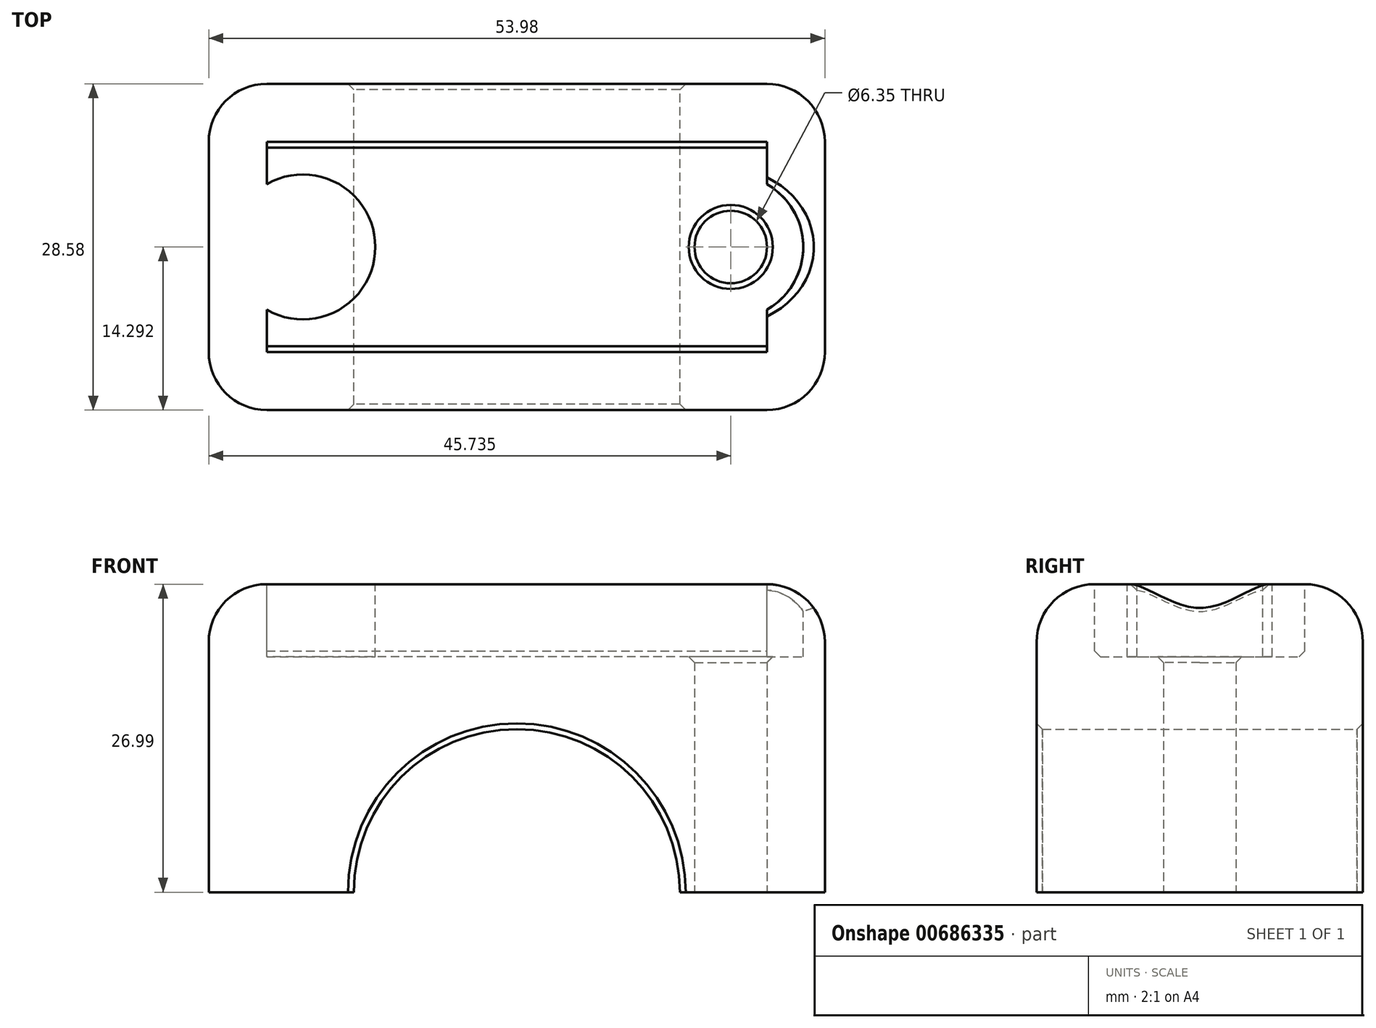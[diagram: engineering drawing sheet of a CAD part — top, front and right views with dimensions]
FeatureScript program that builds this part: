
annotation { "Feature Type Name" : "Feature", "Feature Type Description" : "" }
export const myFeature = defineFeature(function(context is Context, id is Id, definition is map)
    precondition{}
    {
        {
            var Q0;
            Q0=qCreatedBy(makeId("Front.planeOp"),FACE);
            var sketch = newSketch(context, id + "F0", { "sketchPlane" : qUnion([Q0])});
            skArc(sketch, "E0", {"start": v(14.29, 0) * mm, "mid": v(0, 14.29) * mm, "end": v(-14.29, 0) * mm});
            skLineSegment(sketch, "E1", {"start": v(-26.99, 0) * mm, "end": v(-26.99, 26.99) * mm});
            skLineSegment(sketch, "E2", {"start": v(-26.99, 26.99) * mm, "end": v(26.99, 26.99) * mm});
            skLineSegment(sketch, "E3", {"start": v(26.99, 26.99) * mm, "end": v(26.99, 0) * mm});
            skLineSegment(sketch, "E4.trimOffspring", {"start": v(-14.29, 0) * mm, "end": v(-26.99, 0) * mm});
            skLineSegment(sketch, "E5", {"start": v(14.29, 0) * mm, "end": v(26.99, 0) * mm});
            skSolve(sketch);
        }
        {
            var Q0;
            Q0 = qSketchRegion(id + "F0", true);
            extrude(context, id + "F1", {"entities" : qUnion([Q0]), "depth" : 28.57 * mm, "offsetDistance" : 25.4 * mm});
        }
        {
            var Q0;
            Q0=makeQuery(id+"F1.opExtrude","CAP_EDGE",EDGE,{"disambiguationData":[OSD([sQuery(id+"F0.wireOp",EDGE,"E1")])],"isStart":false});
            var Q1;
            Q1=makeQuery(id+"F1.opExtrude","CAP_EDGE",EDGE,{"disambiguationData":[OSD([sQuery(id+"F0.wireOp",EDGE,"E1")])],"isStart":true});
            var Q2;
            Q2=makeQuery(id+"F1.opExtrude","SWEPT_EDGE",EDGE,{"disambiguationData":[OSD([sQuery(id+"F0.wireOp",EDGE,"E1"),sQuery(id+"F0.wireOp",EDGE,"E2")])]});
            var Q3;
            Q3=makeQuery(id+"F1.opExtrude","CAP_EDGE",EDGE,{"disambiguationData":[OSD([sQuery(id+"F0.wireOp",EDGE,"E2")])],"isStart":true});
            var Q4;
            Q4=makeQuery(id+"F1.opExtrude","CAP_EDGE",EDGE,{"disambiguationData":[OSD([sQuery(id+"F0.wireOp",EDGE,"E3")])],"isStart":true});
            var Q5;
            Q5=makeQuery(id+"F1.opExtrude","SWEPT_EDGE",EDGE,{"disambiguationData":[OSD([sQuery(id+"F0.wireOp",EDGE,"E2"),sQuery(id+"F0.wireOp",EDGE,"E3")])]});
            var Q6;
            Q6=makeQuery(id+"F1.opExtrude","CAP_EDGE",EDGE,{"disambiguationData":[OSD([sQuery(id+"F0.wireOp",EDGE,"E3")])],"isStart":false});
            var Q7;
            Q7=makeQuery(id+"F1.opExtrude","CAP_EDGE",EDGE,{"disambiguationData":[OSD([sQuery(id+"F0.wireOp",EDGE,"E2")])],"isStart":false});
            fillet(context, id + "F2", {"entities" : qUnion([Q0, Q1, Q2, Q3, Q4, Q5, Q6, Q7]), "radius" : 5.08 * mm, "tangentPropagation" : true, "allowEdgeOverflow" : false});
        }
        {
            var Q0;
            Q0=makeQuery(id+"F1.opExtrude","CAP_EDGE",EDGE,{"disambiguationData":[OSD([sQuery(id+"F0.wireOp",EDGE,"E0")])],"isStart":false});
            var Q1;
            Q1=makeQuery(id+"F1.opExtrude","CAP_EDGE",EDGE,{"disambiguationData":[OSD([sQuery(id+"F0.wireOp",EDGE,"E0")])],"isStart":true});
            chamfer(context, id + "F3", {"entities" : qUnion([Q0, Q1]), "width" : 0.5 * mm, "tangentPropagation" : true});
        }
        {
            var Q0;
            Q0=makeQuery(id+"F1.opExtrude","SWEPT_FACE",FACE,{"disambiguationData":[OSD([sQuery(id+"F0.wireOp",EDGE,"E5")])]});
            var sketch = newSketch(context, id + "F4", { "sketchPlane" : qUnion([Q0])});
            skLineSegment(sketch, "E6", {"start": v(14.29, 14.29) * mm, "end": v(30.3, 14.29) * mm, "construction": true});
            skLineSegment(sketch, "E7", {"start": v(0, 0) * mm, "end": v(0, -7.99) * mm, "construction": true});
            skCircle(sketch, "E8", {"center": v(18.75, 14.29) * mm, "radius": 3.18 * mm});
            skCircle(sketch, "E9.MirrorC", {"center": v(-18.75, 14.29) * mm, "radius": 3.18 * mm});
            skSolve(sketch);
        }
        {
            var Q0;
            Q0=makeQuery(id+"F4.imprint","IMPRINT",FACE,{"disambiguationData":[TD([[makeQuery(id+"F4.imprint","IMPRINT",EDGE,{"derivedFrom":sQuery(id+"F4.wireOp",EDGE,"E8")}),1.0]])]});
            var Q1;
            Q1=makeQuery(id+"F4.imprint","IMPRINT",FACE,{"disambiguationData":[TD([[makeQuery(id+"F4.imprint","IMPRINT",EDGE,{"derivedFrom":sQuery(id+"F4.wireOp",EDGE,"E9.MirrorC")}),-1.0]])]});
            extrude(context, id + "F5", {"entities" : qUnion([Q0, Q1]), "operationType" : NewBodyOperationType.REMOVE, "oppositeDirection" : true, "depth" : 34.04 * mm, "offsetDistance" : 25.4 * mm});
        }
        {
            var Q0;
            Q0=makeQuery(id+"F1.opExtrude","SWEPT_FACE",FACE,{"disambiguationData":[OSD([sQuery(id+"F0.wireOp",EDGE,"E2")])]});
            var sketch = newSketch(context, id + "F6", { "sketchPlane" : qUnion([Q0])});
            skCircle(sketch, "E10", {"center": v(18.75, -14.29) * mm, "radius": 6.35 * mm});
            skLineSegment(sketch, "E11", {"start": v(0, -19.6) * mm, "end": v(0, 0) * mm, "construction": true});
            skCircle(sketch, "E12.MirrorC", {"center": v(-18.75, -14.29) * mm, "radius": 6.35 * mm});
            skSolve(sketch);
        }
        {
            var Q0;
            {var subQ0=sQuery(id+"F6.wireOp",EDGE,"E12.MirrorC");var subQ1=sQuery(id+"F0.wireOp",EDGE,"E2");var subQ2=makeQuery(id+"F2.opFillet","BLEND_EDGE",EDGE,{"blendedFrom":[makeQuery(id+"F1.opExtrude","SWEPT_EDGE",EDGE,{"disambiguationData":[OSD([sQuery(id+"F0.wireOp",EDGE,"E1"),subQ1])]}),makeQuery(id+"F1.opExtrude","SWEPT_FACE",FACE,{"disambiguationData":[OSD([subQ1])]})],"blendedInto":[makeQuery(id+"F1.opExtrude","SWEPT_FACE",FACE,{"disambiguationData":[OSD([subQ1])]})]});var subQ3=makeQuery(id+"F6.imprint","INTERSECT",VERTEX,{"disambiguationData":[OD(0.0)],"derivedFrom":[subQ2,subQ0]});Q0=makeQuery(id+"F6.imprint","IMPRINT",FACE,{"disambiguationData":[TD([[makeQuery(id+"F6.imprint","IMPRINT",EDGE,{"disambiguationData":[TD([[subQ3,1.0]])],"derivedFrom":subQ0}),-1.0]])]});}
            var Q1;
            {var subQ1=sQuery(id+"F0.wireOp",EDGE,"E2");var subQ2=makeQuery(id+"F1.opExtrude","SWEPT_FACE",FACE,{"disambiguationData":[OSD([subQ1])]});Q1=makeQuery(id+"F6.imprint","IMPRINT",FACE,{"disambiguationData":[TD([[makeQuery(id+"F6.imprint","IMPRINT",EDGE,{"derivedFrom":makeQuery(id+"F5.boolean.opBoolean","INTERSECT",EDGE,{"derivedFrom":[subQ2,makeQuery(id+"F5.opExtrude","SWEPT_FACE",FACE,{"disambiguationData":[OSD([sQuery(id+"F4.wireOp",EDGE,"E8")])]})]})}),-1.0]])]});}
            var Q2;
            {var subQ0=sQuery(id+"F6.wireOp",EDGE,"E10");var subQ1=sQuery(id+"F0.wireOp",EDGE,"E2");var subQ2=makeQuery(id+"F2.opFillet","BLEND_EDGE",EDGE,{"blendedFrom":[makeQuery(id+"F1.opExtrude","SWEPT_EDGE",EDGE,{"disambiguationData":[OSD([subQ1,sQuery(id+"F0.wireOp",EDGE,"E3")])]}),makeQuery(id+"F1.opExtrude","SWEPT_FACE",FACE,{"disambiguationData":[OSD([subQ1])]})],"blendedInto":[makeQuery(id+"F1.opExtrude","SWEPT_FACE",FACE,{"disambiguationData":[OSD([subQ1])]})]});var subQ3=makeQuery(id+"F6.imprint","INTERSECT",VERTEX,{"disambiguationData":[OD(0.0)],"derivedFrom":[subQ2,subQ0]});Q2=makeQuery(id+"F6.imprint","IMPRINT",FACE,{"disambiguationData":[TD([[makeQuery(id+"F6.imprint","IMPRINT",EDGE,{"disambiguationData":[TD([[subQ3,1.0]])],"derivedFrom":subQ0}),1.0]])]});}
            var Q3;
            {var subQ1=sQuery(id+"F0.wireOp",EDGE,"E2");var subQ2=makeQuery(id+"F1.opExtrude","SWEPT_FACE",FACE,{"disambiguationData":[OSD([subQ1])]});Q3=makeQuery(id+"F6.imprint","IMPRINT",FACE,{"disambiguationData":[TD([[makeQuery(id+"F6.imprint","IMPRINT",EDGE,{"derivedFrom":makeQuery(id+"F5.boolean.opBoolean","INTERSECT",EDGE,{"derivedFrom":[subQ2,makeQuery(id+"F5.opExtrude","SWEPT_FACE",FACE,{"disambiguationData":[OSD([sQuery(id+"F4.wireOp",EDGE,"E9.MirrorC")])]})]})}),1.0]])]});}
            extrude(context, id + "F7", {"entities" : qUnion([Q0, Q1, Q2, Q3]), "operationType" : NewBodyOperationType.REMOVE, "oppositeDirection" : true, "depth" : 6.35 * mm, "offsetDistance" : 25.4 * mm});
        }
        {
            var Q0;
            Q0=makeQuery(id+"F7.boolean.opBoolean","COPY",EDGE,{"derivedFrom":makeQuery(id+"F7.opExtrude","CAP_EDGE",EDGE,{"disambiguationData":[OSD([sQuery(id+"F6.wireOp",EDGE,"E12.MirrorC")])],"isStart":true})});
            var Q1;
            {var subQ0=sQuery(id+"F0.wireOp",EDGE,"E2");var subQ1=sQuery(id+"F0.wireOp",EDGE,"E1");Q1=makeQuery(id+"F7.boolean.opBoolean","INTERSECT",EDGE,{"derivedFrom":[makeQuery(id+"F2.opFillet","BLEND_FACE",FACE,{"disambiguationData":[OSD([subQ1,subQ0]),TDD([makeQuery(id+"F1.opExtrude","SWEPT_EDGE",EDGE,{"disambiguationData":[OSD([subQ1,subQ0])]})])]}),makeQuery(id+"F7.opExtrude","SWEPT_FACE",FACE,{"disambiguationData":[OSD([sQuery(id+"F6.wireOp",EDGE,"E12.MirrorC")])]})]});}
            var Q2;
            Q2=makeQuery(id+"F7.boolean.opBoolean","COPY",EDGE,{"derivedFrom":makeQuery(id+"F7.opExtrude","CAP_EDGE",EDGE,{"disambiguationData":[OSD([sQuery(id+"F0.wireOp",EDGE,"E2"),sQuery(id+"F4.wireOp",EDGE,"E9.MirrorC")])],"isStart":false})});
            var Q3;
            Q3=makeQuery(id+"F7.boolean.opBoolean","COPY",EDGE,{"derivedFrom":makeQuery(id+"F7.opExtrude","CAP_EDGE",EDGE,{"disambiguationData":[OSD([sQuery(id+"F0.wireOp",EDGE,"E2"),sQuery(id+"F4.wireOp",EDGE,"E8")])],"isStart":false})});
            var Q4;
            {var subQ0=sQuery(id+"F0.wireOp",EDGE,"E3");var subQ1=sQuery(id+"F0.wireOp",EDGE,"E2");Q4=makeQuery(id+"F7.boolean.opBoolean","INTERSECT",EDGE,{"derivedFrom":[makeQuery(id+"F2.opFillet","BLEND_FACE",FACE,{"disambiguationData":[OSD([subQ1,subQ0]),TDD([makeQuery(id+"F1.opExtrude","SWEPT_EDGE",EDGE,{"disambiguationData":[OSD([subQ1,subQ0])]})])]}),makeQuery(id+"F7.opExtrude","SWEPT_FACE",FACE,{"disambiguationData":[OSD([sQuery(id+"F6.wireOp",EDGE,"E10")])]})]});}
            var Q5;
            Q5=makeQuery(id+"F7.boolean.opBoolean","COPY",EDGE,{"derivedFrom":makeQuery(id+"F7.opExtrude","CAP_EDGE",EDGE,{"disambiguationData":[OSD([sQuery(id+"F6.wireOp",EDGE,"E10")])],"isStart":true})});
            var Q6;
            Q6=makeQuery(id+"F7.boolean.opBoolean","INTERSECT",EDGE,{"derivedFrom":[makeQuery(id+"F5.boolean.opBoolean","COPY",FACE,{"derivedFrom":makeQuery(id+"F5.opExtrude","SWEPT_FACE",FACE,{"disambiguationData":[OSD([sQuery(id+"F4.wireOp",EDGE,"E9.MirrorC")])]})}),makeQuery(id+"F7.opExtrude","CAP_FACE",FACE,{"disambiguationData":[OSD([sQuery(id+"F6.wireOp",EDGE,"E12.MirrorC")])],"isStart":false})]});
            var Q7;
            Q7=makeQuery(id+"F7.boolean.opBoolean","INTERSECT",EDGE,{"derivedFrom":[makeQuery(id+"F5.boolean.opBoolean","COPY",FACE,{"derivedFrom":makeQuery(id+"F5.opExtrude","SWEPT_FACE",FACE,{"disambiguationData":[OSD([sQuery(id+"F4.wireOp",EDGE,"E8")])]})}),makeQuery(id+"F7.opExtrude","CAP_FACE",FACE,{"disambiguationData":[OSD([sQuery(id+"F6.wireOp",EDGE,"E10")])],"isStart":false})]});
            chamfer(context, id + "F8", {"entities" : qUnion([Q0, Q1, Q2, Q3, Q4, Q5, Q6, Q7]), "width" : 0.5 * mm, "tangentPropagation" : true});
        }
    });
